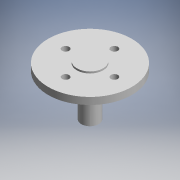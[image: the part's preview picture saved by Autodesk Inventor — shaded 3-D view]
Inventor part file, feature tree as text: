
AUTODESK INVENTOR PART (.ipt)
format: ipt  version: 2017 (Build 210142000, 142)  size: 105,472 bytes
history: native  units: mm (DEFAULTED — no unit token found)
features: extrude x4, sketch x4
ambient origin geometry x8: Origin, YZ Plane, XZ Plane, XY Plane, X Axis, Y Axis, Z Axis, Center Point
bodies: Solid1 (feature_tree)
feature tree (8):
  extrude  "Extrusion1"  Depth=5.0mm
  extrude  "Extrusion2"  Depth=12.0mm
  extrude  "Extrusion4"  Depth=0.5mm
  extrude  "Extrusion5"  Depth=0.5mm
  sketch  "Sketch1"  dims[d3=0.0mm d4=5.0mm]
  sketch  "Sketch2"  dims[d5=12.0mm d6=0.0mm d12=7.5mm]
  sketch  "Sketch4"  dims[d13=0.5mm d14=0.0mm d16=7.0mm]
  sketch  "Sketch5"  dims[d18=0.5mm d19=0.0mm d20=7.0mm d21=7.0mm]
